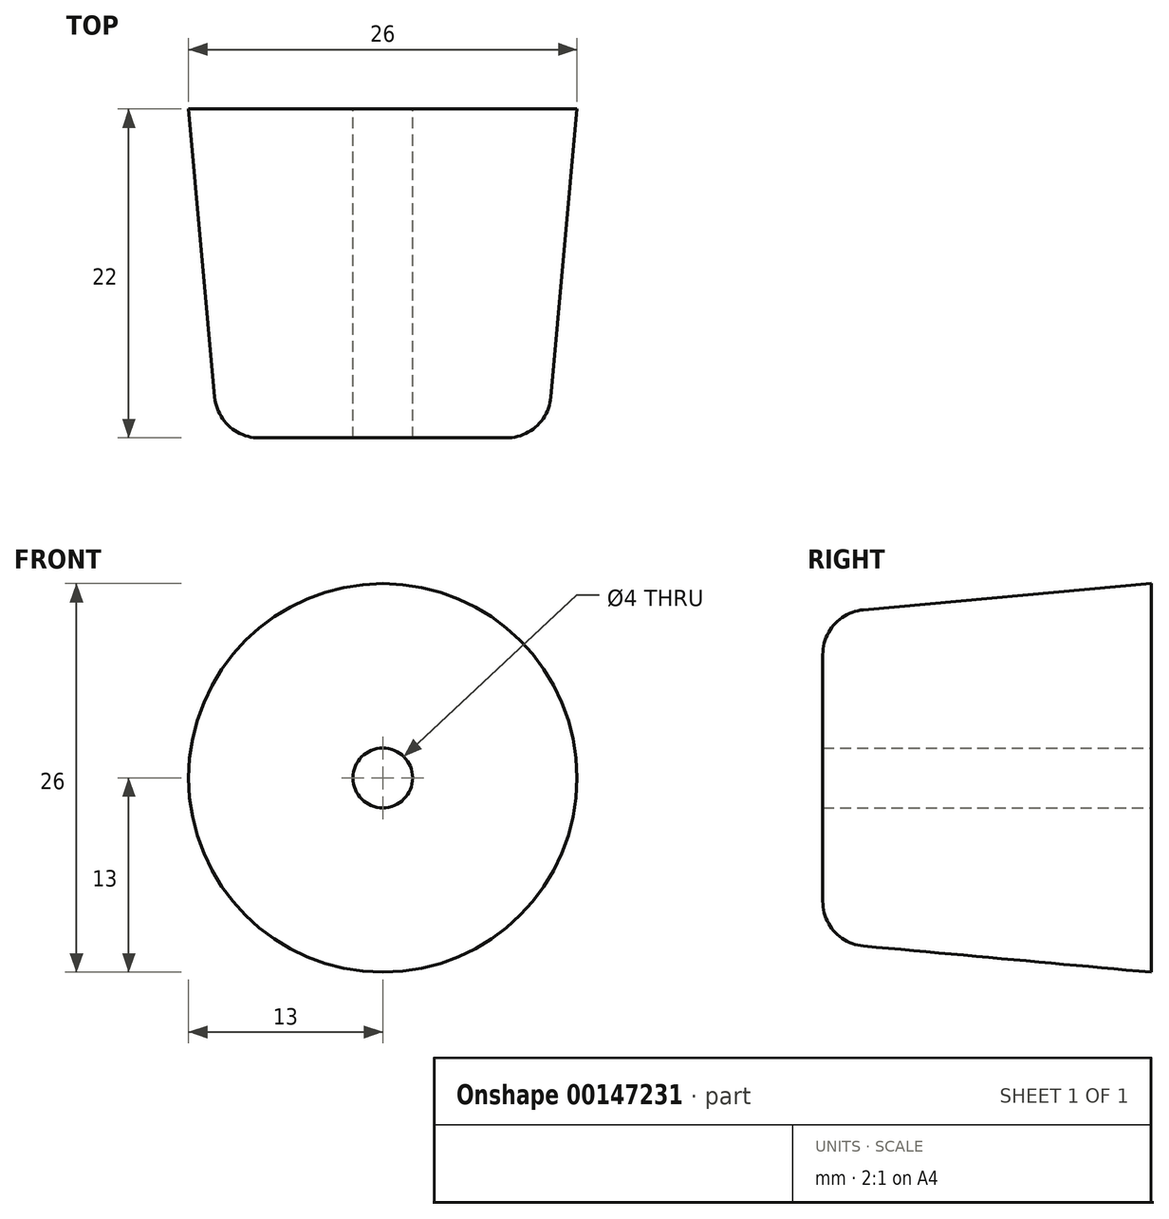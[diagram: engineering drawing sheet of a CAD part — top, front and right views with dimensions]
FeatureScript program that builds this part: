
annotation { "Feature Type Name" : "Feature", "Feature Type Description" : "" }
export const myFeature = defineFeature(function(context is Context, id is Id, definition is map)
    precondition{}
    {
        {
            var Q0;
            Q0=qCreatedBy(makeId("Front.planeOp"),FACE);
            var sketch = newSketch(context, id + "F0", { "sketchPlane" : qUnion([Q0])});
            skCircle(sketch, "E0", {"center": v(0, 0) * mm, "radius": 13 * mm});
            skSolve(sketch);
        }
        {
            var Q0;
            Q0=qCreatedBy(makeId("Front.planeOp"),FACE);
            cPlane(context, id + "F1", {"entities" : qUnion([Q0]), "cplaneType" : CPlaneType.OFFSET, "offset" : 22 * mm, "width" : 150 * mm, "height" : 150 * mm});
        }
        {
            var Q0;
            Q0=qCreatedBy(id+"F1.planeOp",FACE);
            var sketch = newSketch(context, id + "F2", { "sketchPlane" : qUnion([Q0])});
            skCircle(sketch, "E1", {"center": v(0, 0) * mm, "radius": 11 * mm});
            skSolve(sketch);
        }
        {
            var Q0;
            Q0 = qSketchRegion(id + "F0", true);
            var Q1;
            Q1 = qSketchRegion(id + "F2", true);
            loft(context, id + "F3", {"sheetProfilesArray" : [{ "sheetProfileEntities" : qUnion([Q0]) }, { "sheetProfileEntities" : qUnion([Q1]) }]});
        }
        {
            var Q0;
            Q0=makeQuery(id+"F3.opLoft","MID_CAP_EDGE",EDGE,{"disambiguationData":[OSD([sQuery(id+"F0.wireOp",EDGE,"E0"),sQuery(id+"F2.wireOp",EDGE,"E1")])],"capPos":1.0});
            fillet(context, id + "F4", {"entities" : qUnion([Q0]), "radius" : 3 * mm, "tangentPropagation" : true, "allowEdgeOverflow" : false});
        }
        {
            var Q0;
            Q0=qCreatedBy(makeId("Front.planeOp"),FACE);
            var sketch = newSketch(context, id + "F5", { "sketchPlane" : qUnion([Q0])});
            skCircle(sketch, "E2", {"center": v(0, 0) * mm, "radius": 2 * mm});
            skSolve(sketch);
        }
        {
            var Q0;
            Q0 = qSketchRegion(id + "F5", true);
            extrude(context, id + "F6", {"entities" : qUnion([Q0]), "operationType" : NewBodyOperationType.REMOVE, "endBound" : BoundingType.THROUGH_ALL, "depth" : 25 * mm});
        }
    });
